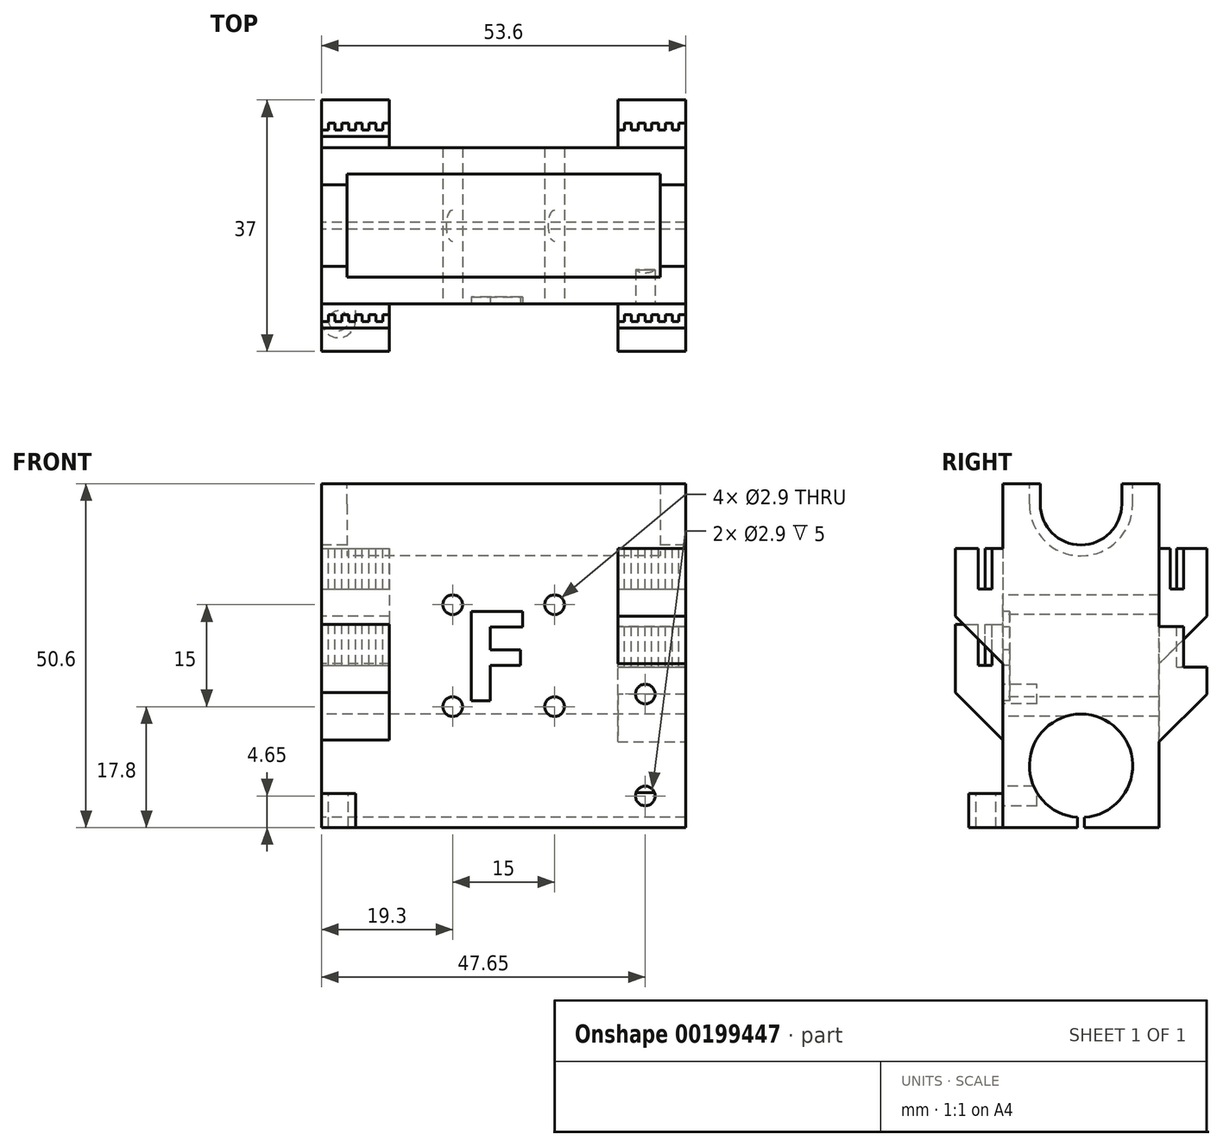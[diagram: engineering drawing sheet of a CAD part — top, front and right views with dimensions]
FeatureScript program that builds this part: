
annotation { "Feature Type Name" : "Feature", "Feature Type Description" : "" }
export const myFeature = defineFeature(function(context is Context, id is Id, definition is map)
    precondition{}
    {
        {
            assignVariable(context, id + "F0", {"name" : "LM8LUU", "anyValue" : 1.8});
        }
        {
            var Q0;
            Q0=qCreatedBy(makeId("Top.planeOp"),FACE);
            var sketch = newSketch(context, id + "F1", { "sketchPlane" : qUnion([Q0])});
            skLineSegment(sketch, "E0.bottom", {"start": v(0, 0) * mm, "end": v(53.6, 0) * mm});
            skLineSegment(sketch, "E0.top", {"start": v(0, 23) * mm, "end": v(53.6, 23) * mm});
            skLineSegment(sketch, "E0.left", {"start": v(0, 0) * mm, "end": v(0, 23) * mm});
            skLineSegment(sketch, "E0.right", {"start": v(53.6, 0) * mm, "end": v(53.6, 23) * mm});
            skSolve(sketch);
        }
        {
            var Q0;
            Q0=qSketchRegion(id+"F1",true);
            extrude(context, id + "F2", {"entities" : qUnion([Q0]), "depth" : 50.6 * mm});
        }
        {
            var Q0;
            Q0=makeQuery(id+"F2.opExtrude","SWEPT_FACE",FACE,{"disambiguationData":[OSD([sQuery(id+"F1.wireOp",EDGE,"E0.left")])]});
            var sketch = newSketch(context, id + "F3", { "sketchPlane" : qUnion([Q0])});
            skCircle(sketch, "E1", {"center": v(-11.5, 9.1) * mm, "radius": 7.6 * mm});
            skCircle(sketch, "E2", {"center": v(-11.5, 47.6) * mm, "radius": 6 * mm});
            skLineSegment(sketch, "E3", {"start": v(-23, 47.6) * mm, "end": v(0, 47.6) * mm, "construction": true});
            skLineSegment(sketch, "E4", {"start": v(-17.5, 50.6) * mm, "end": v(-17.5, 47.6) * mm});
            skLineSegment(sketch, "E5", {"start": v(-5.5, 50.6) * mm, "end": v(-5.5, 47.6) * mm});
            skLineSegment(sketch, "E6", {"start": v(-23, 9.1) * mm, "end": v(0, 9.1) * mm, "construction": true});
            skLineSegment(sketch, "E7", {"start": v(-11.5, 9.1) * mm, "end": v(-11.5, 0) * mm, "construction": true});
            skLineSegment(sketch, "E8", {"start": v(-11.5, 0) * mm, "end": v(-12, 0) * mm});
            skLineSegment(sketch, "E9", {"start": v(-12, 0) * mm, "end": v(-12, 1.52) * mm});
            skLineSegment(sketch, "E10", {"start": v(-12, 1.52) * mm, "end": v(-11, 1.52) * mm});
            skLineSegment(sketch, "E11", {"start": v(-11, 1.52) * mm, "end": v(-11, 0) * mm});
            skLineSegment(sketch, "E12", {"start": v(-11, 0) * mm, "end": v(-11.5, 0) * mm});
            skCircle(sketch, "E13", {"center": v(-11.5, 47.6) * mm, "radius": 7.6 * mm});
            skLineSegment(sketch, "E14", {"start": v(-3.9, 47.6) * mm, "end": v(-3.9, 50.6) * mm});
            skLineSegment(sketch, "E15", {"start": v(-19.1, 47.6) * mm, "end": v(-19.1, 50.6) * mm});
            skSolve(sketch);
        }
        {
            var Q0;
            {var subQ0=sQuery(id+"F3.wireOp",EDGE,"61a55092-bd36-442a-954f-b1d305e603b2");var subQ1=sQuery(id+"F3.wireOp",EDGE,"E1");var subQ3=makeQuery(id+"F3.imprint","INTERSECT",VERTEX,{"disambiguationData":[OD(0.0)],"derivedFrom":[subQ1,subQ0]});Q0=makeQuery(id+"F3.imprint","IMPRINT",FACE,{"disambiguationData":[TD([[makeQuery(id+"F3.imprint","IMPRINT",EDGE,{"disambiguationData":[TD([[subQ3,-1.0]])],"derivedFrom":subQ1}),1.0]])]});}
            var Q1;
            {var subQ0=sQuery(id+"F3.wireOp",EDGE,"ccdeb851-c584-4ba8-b480-4501c20c5f95");var subQ1=sQuery(id+"F3.wireOp",EDGE,"E1");var subQ3=makeQuery(id+"F3.imprint","INTERSECT",VERTEX,{"disambiguationData":[OD(0.0)],"derivedFrom":[subQ1,subQ0]});Q1=makeQuery(id+"F3.imprint","IMPRINT",FACE,{"disambiguationData":[TD([[makeQuery(id+"F3.imprint","IMPRINT",EDGE,{"disambiguationData":[TD([[subQ3,1.0]])],"derivedFrom":subQ1}),1.0]])]});}
            var Q2;
            Q2=makeQuery(id+"F3.imprint","IMPRINT",FACE,{"disambiguationData":[TD([[makeQuery(id+"F3.imprint","IMPRINT",EDGE,{"derivedFrom":sQuery(id+"F3.wireOp",EDGE,"E8")}),-1.0]])]});
            var Q3;
            {var subQ0=sQuery(id+"F3.wireOp",EDGE,"E10");Q3=makeQuery(id+"F3.imprint","IMPRINT",FACE,{"disambiguationData":[TD([[makeQuery(id+"F3.imprint","IMPRINT",EDGE,{"derivedFrom":subQ0}),-1.0]])]});}
            var Q4;
            {var subQ3=sQuery(id+"F3.wireOp",EDGE,"84843404-b723-4df1-a710-1511c094684b");Q4=makeQuery(id+"F3.imprint","IMPRINT",FACE,{"disambiguationData":[TD([[makeQuery(id+"F3.imprint","IMPRINT",EDGE,{"derivedFrom":subQ3}),-1.0]])]});}
            var Q5;
            {var subQ3=sQuery(id+"F3.wireOp",EDGE,"84843404-b723-4df1-a710-1511c094684b");Q5=makeQuery(id+"F3.imprint","IMPRINT",FACE,{"disambiguationData":[TD([[makeQuery(id+"F3.imprint","IMPRINT",EDGE,{"derivedFrom":subQ3}),1.0]])]});}
            var Q6;
            {var subQ7=sQuery(id+"F3.wireOp",EDGE,"E10");Q6=makeQuery(id+"F3.imprint","IMPRINT",FACE,{"disambiguationData":[TD([[makeQuery(id+"F3.imprint","IMPRINT",EDGE,{"derivedFrom":subQ7}),1.0]])]});}
            var Q7;
            {var subQ3=sQuery(id+"F3.wireOp",EDGE,"E5");Q7=makeQuery(id+"F3.imprint","IMPRINT",FACE,{"disambiguationData":[TD([[makeQuery(id+"F3.imprint","IMPRINT",EDGE,{"derivedFrom":subQ3}),-1.0]])]});}
            var Q8;
            {var subQ0=sQuery(id+"F3.wireOp",EDGE,"E4");Q8=makeQuery(id+"F3.imprint","IMPRINT",FACE,{"disambiguationData":[TD([[makeQuery(id+"F3.imprint","IMPRINT",EDGE,{"derivedFrom":subQ0}),1.0]])]});}
            var Q9;
            {var subQ0=sQuery(id+"F3.wireOp",EDGE,"E4");Q9=makeQuery(id+"F3.imprint","IMPRINT",FACE,{"disambiguationData":[TD([[makeQuery(id+"F3.imprint","IMPRINT",EDGE,{"derivedFrom":subQ0}),1.0]])]});}
            var Q10;
            {var subQ3=sQuery(id+"F3.wireOp",EDGE,"E5");Q10=makeQuery(id+"F3.imprint","IMPRINT",FACE,{"disambiguationData":[TD([[makeQuery(id+"F3.imprint","IMPRINT",EDGE,{"derivedFrom":subQ3}),-1.0]])]});}
            var Q11;
            {var subQ1=sQuery(id+"F3.wireOp",EDGE,"E2");var subQ4=makeQuery(id+"F3.imprint","INTERSECT",VERTEX,{"derivedFrom":[subQ1,sQuery(id+"F3.wireOp",EDGE,"E5")]});Q11=makeQuery(id+"F3.imprint","IMPRINT",FACE,{"disambiguationData":[TD([[makeQuery(id+"F3.imprint","IMPRINT",EDGE,{"disambiguationData":[TD([[subQ4,-1.0]])],"derivedFrom":subQ1}),1.0]])]});}
            extrude(context, id + "F4", {"entities" : qUnion([Q0, Q1, Q2, Q3, Q4, Q5, Q6, Q7, Q8, Q9, Q10, Q11]), "operationType" : NewBodyOperationType.REMOVE, "endBound" : BoundingType.THROUGH_ALL, "oppositeDirection" : true, "depth" : 25 * mm});
        }
        {
            var Q0;
            {var subQ3=sQuery(id+"F3.wireOp",EDGE,"E4");Q0=makeQuery(id+"F3.imprint","IMPRINT",FACE,{"disambiguationData":[TD([[makeQuery(id+"F3.imprint","IMPRINT",EDGE,{"derivedFrom":subQ3}),-1.0]])]});}
            var Q1;
            {var subQ3=sQuery(id+"F3.wireOp",EDGE,"E15");Q1=makeQuery(id+"F3.imprint","IMPRINT",FACE,{"disambiguationData":[TD([[makeQuery(id+"F3.imprint","IMPRINT",EDGE,{"derivedFrom":subQ3}),-1.0]])]});}
            var Q2;
            {var subQ3=sQuery(id+"F3.wireOp",EDGE,"E14");Q2=makeQuery(id+"F3.imprint","IMPRINT",FACE,{"disambiguationData":[TD([[makeQuery(id+"F3.imprint","IMPRINT",EDGE,{"derivedFrom":subQ3}),1.0]])]});}
            extrude(context, id + "F5", {"entities" : qUnion([Q0, Q1, Q2]), "operationType" : NewBodyOperationType.REMOVE, "oppositeDirection" : true, "depth" : (46.25 + getVariable(context, 'LM8LUU') * 2) * mm});
        }
        {
            var Q0;
            {var subQ3=sQuery(id+"F3.wireOp",EDGE,"E4");Q0=makeQuery(id+"F3.imprint","IMPRINT",FACE,{"disambiguationData":[TD([[makeQuery(id+"F3.imprint","IMPRINT",EDGE,{"derivedFrom":subQ3}),-1.0]])]});}
            var Q1;
            {var subQ3=sQuery(id+"F3.wireOp",EDGE,"E15");Q1=makeQuery(id+"F3.imprint","IMPRINT",FACE,{"disambiguationData":[TD([[makeQuery(id+"F3.imprint","IMPRINT",EDGE,{"derivedFrom":subQ3}),-1.0]])]});}
            var Q2;
            {var subQ3=sQuery(id+"F3.wireOp",EDGE,"E14");Q2=makeQuery(id+"F3.imprint","IMPRINT",FACE,{"disambiguationData":[TD([[makeQuery(id+"F3.imprint","IMPRINT",EDGE,{"derivedFrom":subQ3}),1.0]])]});}
            extrude(context, id + "F6", {"entities" : qUnion([Q0, Q1, Q2]), "operationType" : NewBodyOperationType.ADD, "oppositeDirection" : true, "depth" : (26.75 - getVariable(context, 'LM8LUU')) * mm});
        }
        {
            var Q0;
            {var subQ3=sQuery(id+"F3.wireOp",EDGE,"E4");Q0=makeQuery(id+"F3.imprint","IMPRINT",FACE,{"disambiguationData":[TD([[makeQuery(id+"F3.imprint","IMPRINT",EDGE,{"derivedFrom":subQ3}),-1.0]])]});}
            var Q1;
            {var subQ3=sQuery(id+"F3.wireOp",EDGE,"E15");Q1=makeQuery(id+"F3.imprint","IMPRINT",FACE,{"disambiguationData":[TD([[makeQuery(id+"F3.imprint","IMPRINT",EDGE,{"derivedFrom":subQ3}),-1.0]])]});}
            var Q2;
            {var subQ3=sQuery(id+"F3.wireOp",EDGE,"E14");Q2=makeQuery(id+"F3.imprint","IMPRINT",FACE,{"disambiguationData":[TD([[makeQuery(id+"F3.imprint","IMPRINT",EDGE,{"derivedFrom":subQ3}),1.0]])]});}
            extrude(context, id + "F7", {"entities" : qUnion([Q0, Q1, Q2]), "operationType" : NewBodyOperationType.REMOVE, "oppositeDirection" : true, "depth" : (23.25 + getVariable(context, 'LM8LUU')) * mm});
        }
        {
            var Q0;
            {var subQ3=sQuery(id+"F3.wireOp",EDGE,"E4");Q0=makeQuery(id+"F3.imprint","IMPRINT",FACE,{"disambiguationData":[TD([[makeQuery(id+"F3.imprint","IMPRINT",EDGE,{"derivedFrom":subQ3}),-1.0]])]});}
            var Q1;
            {var subQ3=sQuery(id+"F3.wireOp",EDGE,"E15");Q1=makeQuery(id+"F3.imprint","IMPRINT",FACE,{"disambiguationData":[TD([[makeQuery(id+"F3.imprint","IMPRINT",EDGE,{"derivedFrom":subQ3}),-1.0]])]});}
            var Q2;
            {var subQ3=sQuery(id+"F3.wireOp",EDGE,"E14");Q2=makeQuery(id+"F3.imprint","IMPRINT",FACE,{"disambiguationData":[TD([[makeQuery(id+"F3.imprint","IMPRINT",EDGE,{"derivedFrom":subQ3}),1.0]])]});}
            extrude(context, id + "F8", {"entities" : qUnion([Q0, Q1, Q2]), "operationType" : NewBodyOperationType.ADD, "oppositeDirection" : true, "depth" : 3.75 * mm});
        }
        {
            var Q0;
            Q0=makeQuery(id+"F2.opExtrude","SWEPT_FACE",FACE,{"disambiguationData":[OSD([sQuery(id+"F1.wireOp",EDGE,"E0.bottom")])]});
            var sketch = newSketch(context, id + "F9", { "sketchPlane" : qUnion([Q0])});
            skLineSegment(sketch, "E16.bottom", {"start": v(0, 29.9) * mm, "end": v(10, 29.9) * mm});
            skLineSegment(sketch, "E16.top", {"start": v(0, 9.9) * mm, "end": v(10, 9.9) * mm});
            skLineSegment(sketch, "E16.left", {"start": v(0, 29.9) * mm, "end": v(0, 9.9) * mm});
            skLineSegment(sketch, "E16.right", {"start": v(10, 29.9) * mm, "end": v(10, 9.9) * mm});
            skLineSegment(sketch, "E17.bottom", {"start": v(53.6, 41.1) * mm, "end": v(43.6, 41.1) * mm});
            skLineSegment(sketch, "E17.top", {"start": v(53.6, 21.1) * mm, "end": v(43.6, 21.1) * mm});
            skLineSegment(sketch, "E17.left", {"start": v(53.6, 41.1) * mm, "end": v(53.6, 21.1) * mm});
            skLineSegment(sketch, "E17.right", {"start": v(43.6, 41.1) * mm, "end": v(43.6, 21.1) * mm});
            skPoint(sketch, "E18", {"position": v(0, 47.6) * mm});
            skPoint(sketch, "E19", {"position": v(0, 9.4) * mm});
            skSolve(sketch);
        }
        {
            var Q0;
            Q0=qSketchRegion(id+"F9",true);
            extrude(context, id + "F10", {"entities" : qUnion([Q0]), "operationType" : NewBodyOperationType.ADD, "depth" : 7 * mm});
        }
        {
            var Q0;
            Q0=makeQuery(id+"F10.opExtrude","CAP_EDGE",EDGE,{"disambiguationData":[OSD([sQuery(id+"F9.wireOp",EDGE,"E16.top")])],"isStart":false});
            var Q1;
            Q1=makeQuery(id+"F10.opExtrude","CAP_EDGE",EDGE,{"disambiguationData":[OSD([sQuery(id+"F9.wireOp",EDGE,"E17.top")])],"isStart":false});
            chamfer(context, id + "F11", {"entities" : qUnion([Q0, Q1]), "width" : 10 * mm, "tangentPropagation" : true});
        }
        {
            var Q0;
            Q0=makeQuery(id+"F10.opExtrude","SWEPT_FACE",FACE,{"disambiguationData":[OSD([sQuery(id+"F9.wireOp",EDGE,"E16.bottom")])]});
            var sketch = newSketch(context, id + "F12", { "sketchPlane" : qUnion([Q0])});
            skLineSegment(sketch, "E20", {"start": v(-935.9, 0) * mm, "end": v(-935.88, -4.54) * mm});
            skLineSegment(sketch, "E21.left", {"start": v(0, -3.6) * mm, "end": v(0, -1.6) * mm});
            skLineSegment(sketch, "E22", {"start": v(6, -2.6) * mm, "end": v(7, -2.6) * mm});
            skLineSegment(sketch, "E23", {"start": v(4, -2.6) * mm, "end": v(5, -2.6) * mm});
            skLineSegment(sketch, "E24", {"start": v(0, -2.6) * mm, "end": v(1, -2.6) * mm});
            skLineSegment(sketch, "E25", {"start": v(7, -1.6) * mm, "end": v(8, -1.6) * mm});
            skLineSegment(sketch, "E26", {"start": v(2, -2.6) * mm, "end": v(3, -2.6) * mm});
            skLineSegment(sketch, "E27", {"start": v(3, -1.6) * mm, "end": v(4, -1.6) * mm});
            skLineSegment(sketch, "E28", {"start": v(8, -2.6) * mm, "end": v(9, -2.6) * mm});
            skLineSegment(sketch, "E29", {"start": v(8, -1.6) * mm, "end": v(8, -2.6) * mm});
            skLineSegment(sketch, "E30", {"start": v(9, -2.6) * mm, "end": v(9, -1.6) * mm});
            skLineSegment(sketch, "E31", {"start": v(10, -1.6) * mm, "end": v(10, -2.6) * mm});
            skLineSegment(sketch, "E32", {"start": v(6, -1.6) * mm, "end": v(6, -2.6) * mm});
            skLineSegment(sketch, "E33", {"start": v(2, -1.6) * mm, "end": v(2, -2.6) * mm});
            skLineSegment(sketch, "E34", {"start": v(1, -1.6) * mm, "end": v(2, -1.6) * mm});
            skLineSegment(sketch, "E35", {"start": v(1, -2.6) * mm, "end": v(1, -1.6) * mm});
            skLineSegment(sketch, "E36", {"start": v(9, -1.6) * mm, "end": v(10, -1.6) * mm});
            skLineSegment(sketch, "E37", {"start": v(5, -1.6) * mm, "end": v(6, -1.6) * mm});
            skLineSegment(sketch, "E38", {"start": v(5, -2.6) * mm, "end": v(5, -1.6) * mm});
            skLineSegment(sketch, "E39", {"start": v(3, -2.6) * mm, "end": v(3, -1.6) * mm});
            skLineSegment(sketch, "E40", {"start": v(4, -1.6) * mm, "end": v(4, -2.6) * mm});
            skLineSegment(sketch, "E41", {"start": v(7, -2.6) * mm, "end": v(7, -1.6) * mm});
            skLineSegment(sketch, "E42", {"start": v(0, -1.6) * mm, "end": v(0, -2.6) * mm});
            skLineSegment(sketch, "E43", {"start": v(10, -2.6) * mm, "end": v(10, -3.6) * mm});
            skLineSegment(sketch, "E44", {"start": v(0, -3.6) * mm, "end": v(10, -3.6) * mm});
            skLineSegment(sketch, "E45", {"start": v(5.3, -1.6) * mm, "end": v(5.3, 0) * mm});
            skSolve(sketch);
        }
        {
            var Q0;
            Q0=qSketchRegion(id+"F12",true);
            extrude(context, id + "F13", {"entities" : qUnion([Q0]), "operationType" : NewBodyOperationType.REMOVE, "oppositeDirection" : true, "depth" : 6 * mm});
        }
        {
            var Q0;
            Q0=makeQuery(id+"F10.opExtrude","SWEPT_FACE",FACE,{"disambiguationData":[OSD([sQuery(id+"F9.wireOp",EDGE,"E17.bottom")])]});
            var sketch = newSketch(context, id + "F14", { "sketchPlane" : qUnion([Q0])});
            skLineSegment(sketch, "E46.left", {"start": v(43.6, -3.6) * mm, "end": v(43.6, -1.6) * mm});
            skLineSegment(sketch, "E47", {"start": v(49.6, -2.6) * mm, "end": v(50.6, -2.6) * mm});
            skLineSegment(sketch, "E48", {"start": v(47.6, -2.6) * mm, "end": v(48.6, -2.6) * mm});
            skLineSegment(sketch, "E49", {"start": v(43.6, -2.6) * mm, "end": v(44.6, -2.6) * mm});
            skLineSegment(sketch, "E50", {"start": v(50.6, -1.6) * mm, "end": v(51.6, -1.6) * mm});
            skLineSegment(sketch, "E51", {"start": v(45.6, -2.6) * mm, "end": v(46.6, -2.6) * mm});
            skLineSegment(sketch, "E52", {"start": v(46.6, -1.6) * mm, "end": v(47.6, -1.6) * mm});
            skLineSegment(sketch, "E53", {"start": v(51.6, -2.6) * mm, "end": v(52.6, -2.6) * mm});
            skLineSegment(sketch, "E54", {"start": v(51.6, -1.6) * mm, "end": v(51.6, -2.6) * mm});
            skLineSegment(sketch, "E55", {"start": v(52.6, -2.6) * mm, "end": v(52.6, -1.6) * mm});
            skLineSegment(sketch, "E56", {"start": v(53.6, -1.6) * mm, "end": v(53.6, -2.6) * mm});
            skLineSegment(sketch, "E57", {"start": v(49.6, -1.6) * mm, "end": v(49.6, -2.6) * mm});
            skLineSegment(sketch, "E58", {"start": v(45.6, -1.6) * mm, "end": v(45.6, -2.6) * mm});
            skLineSegment(sketch, "E59", {"start": v(44.6, -1.6) * mm, "end": v(45.6, -1.6) * mm});
            skLineSegment(sketch, "E60", {"start": v(44.6, -2.6) * mm, "end": v(44.6, -1.6) * mm});
            skLineSegment(sketch, "E61", {"start": v(52.6, -1.6) * mm, "end": v(53.6, -1.6) * mm});
            skLineSegment(sketch, "E62", {"start": v(48.6, -1.6) * mm, "end": v(49.6, -1.6) * mm});
            skLineSegment(sketch, "E63", {"start": v(48.6, -2.6) * mm, "end": v(48.6, -1.6) * mm});
            skLineSegment(sketch, "E64", {"start": v(46.6, -2.6) * mm, "end": v(46.6, -1.6) * mm});
            skLineSegment(sketch, "E65", {"start": v(47.6, -1.6) * mm, "end": v(47.6, -2.6) * mm});
            skLineSegment(sketch, "E66", {"start": v(50.6, -2.6) * mm, "end": v(50.6, -1.6) * mm});
            skLineSegment(sketch, "E67", {"start": v(43.6, -1.6) * mm, "end": v(43.6, -2.6) * mm});
            skLineSegment(sketch, "E68", {"start": v(53.6, -2.6) * mm, "end": v(53.6, -3.6) * mm});
            skLineSegment(sketch, "E69", {"start": v(43.6, -3.6) * mm, "end": v(53.6, -3.6) * mm});
            skLineSegment(sketch, "E70", {"start": v(48.83, -1.6) * mm, "end": v(48.83, 0) * mm});
            skSolve(sketch);
        }
        {
            var Q0;
            Q0=qSketchRegion(id+"F14",true);
            extrude(context, id + "F15", {"entities" : qUnion([Q0]), "operationType" : NewBodyOperationType.REMOVE, "oppositeDirection" : true, "depth" : 6 * mm});
        }
        {
            var Q0;
            Q0=makeQuery(id+"F2.opExtrude","SWEPT_FACE",FACE,{"disambiguationData":[OSD([sQuery(id+"F1.wireOp",EDGE,"E0.top")])]});
            var sketch = newSketch(context, id + "F16", { "sketchPlane" : qUnion([Q0])});
            skLineSegment(sketch, "E71.bottom", {"start": v(-53.6, 9.6) * mm, "end": v(-43.6, 9.6) * mm});
            skLineSegment(sketch, "E71.top", {"start": v(-53.6, 29.6) * mm, "end": v(-43.6, 29.6) * mm});
            skLineSegment(sketch, "E71.left", {"start": v(-53.6, 9.6) * mm, "end": v(-53.6, 29.6) * mm});
            skLineSegment(sketch, "E71.right", {"start": v(-43.6, 9.6) * mm, "end": v(-43.6, 29.6) * mm});
            skLineSegment(sketch, "E72.bottom", {"start": v(0, 41.1) * mm, "end": v(-10, 41.1) * mm});
            skLineSegment(sketch, "E72.top", {"start": v(0, 21.1) * mm, "end": v(-10, 21.1) * mm});
            skLineSegment(sketch, "E72.left", {"start": v(0, 41.1) * mm, "end": v(0, 21.1) * mm});
            skLineSegment(sketch, "E72.right", {"start": v(-10, 41.1) * mm, "end": v(-10, 21.1) * mm});
            skSolve(sketch);
        }
        {
            var Q0;
            Q0=qSketchRegion(id+"F16",true);
            extrude(context, id + "F17", {"entities" : qUnion([Q0]), "operationType" : NewBodyOperationType.ADD, "depth" : 7 * mm});
        }
        {
            var Q0;
            Q0=makeQuery(id+"F17.opExtrude","SWEPT_FACE",FACE,{"disambiguationData":[OSD([sQuery(id+"F16.wireOp",EDGE,"E71.top")])]});
            var sketch = newSketch(context, id + "F18", { "sketchPlane" : qUnion([Q0])});
            skLineSegment(sketch, "E73.left", {"start": v(43.6, 24.6) * mm, "end": v(43.6, 26.6) * mm});
            skLineSegment(sketch, "E74", {"start": v(49.6, 25.6) * mm, "end": v(50.6, 25.6) * mm});
            skLineSegment(sketch, "E75", {"start": v(47.6, 25.6) * mm, "end": v(48.6, 25.6) * mm});
            skLineSegment(sketch, "E76", {"start": v(43.6, 25.6) * mm, "end": v(44.6, 25.6) * mm});
            skLineSegment(sketch, "E77", {"start": v(50.6, 26.6) * mm, "end": v(51.6, 26.6) * mm});
            skLineSegment(sketch, "E78", {"start": v(45.6, 25.6) * mm, "end": v(46.6, 25.6) * mm});
            skLineSegment(sketch, "E79", {"start": v(46.6, 26.6) * mm, "end": v(47.6, 26.6) * mm});
            skLineSegment(sketch, "E80", {"start": v(51.6, 25.6) * mm, "end": v(52.6, 25.6) * mm});
            skLineSegment(sketch, "E81", {"start": v(51.6, 26.6) * mm, "end": v(51.6, 25.6) * mm});
            skLineSegment(sketch, "E82", {"start": v(52.6, 25.6) * mm, "end": v(52.6, 26.6) * mm});
            skLineSegment(sketch, "E83", {"start": v(53.6, 26.6) * mm, "end": v(53.6, 25.6) * mm});
            skLineSegment(sketch, "E84", {"start": v(49.6, 26.6) * mm, "end": v(49.6, 25.6) * mm});
            skLineSegment(sketch, "E85", {"start": v(45.6, 26.6) * mm, "end": v(45.6, 25.6) * mm});
            skLineSegment(sketch, "E86", {"start": v(44.6, 26.6) * mm, "end": v(45.6, 26.6) * mm});
            skLineSegment(sketch, "E87", {"start": v(44.6, 25.6) * mm, "end": v(44.6, 26.6) * mm});
            skLineSegment(sketch, "E88", {"start": v(52.6, 26.6) * mm, "end": v(53.6, 26.6) * mm});
            skLineSegment(sketch, "E89", {"start": v(48.6, 26.6) * mm, "end": v(49.6, 26.6) * mm});
            skLineSegment(sketch, "E90", {"start": v(48.6, 25.6) * mm, "end": v(48.6, 26.6) * mm});
            skLineSegment(sketch, "E91", {"start": v(46.6, 25.6) * mm, "end": v(46.6, 26.6) * mm});
            skLineSegment(sketch, "E92", {"start": v(47.6, 26.6) * mm, "end": v(47.6, 25.6) * mm});
            skLineSegment(sketch, "E93", {"start": v(50.6, 25.6) * mm, "end": v(50.6, 26.6) * mm});
            skLineSegment(sketch, "E94", {"start": v(43.6, 26.6) * mm, "end": v(43.6, 25.6) * mm});
            skLineSegment(sketch, "E95", {"start": v(53.6, 25.6) * mm, "end": v(53.6, 24.6) * mm});
            skLineSegment(sketch, "E96", {"start": v(43.6, 24.6) * mm, "end": v(53.6, 24.6) * mm});
            skLineSegment(sketch, "E97", {"start": v(48.6, 24.6) * mm, "end": v(48.6, 23) * mm});
            skSolve(sketch);
        }
        {
            var Q0;
            {var subQ4=sQuery(id+"F18.wireOp",EDGE,"E73.left");Q0=makeQuery(id+"F18.imprint","IMPRINT",FACE,{"disambiguationData":[TD([[makeQuery(id+"F18.imprint","IMPRINT",EDGE,{"derivedFrom":subQ4}),1.0]])]});}
            extrude(context, id + "F19", {"entities" : qUnion([Q0]), "operationType" : NewBodyOperationType.REMOVE, "oppositeDirection" : true, "depth" : 6 * mm});
        }
        {
            var Q0;
            Q0=makeQuery(id+"F17.opExtrude","SWEPT_FACE",FACE,{"disambiguationData":[OSD([sQuery(id+"F16.wireOp",EDGE,"E72.bottom")])]});
            var sketch = newSketch(context, id + "F20", { "sketchPlane" : qUnion([Q0])});
            skLineSegment(sketch, "E98", {"start": v(6, 25.6) * mm, "end": v(7, 25.6) * mm});
            skLineSegment(sketch, "E99", {"start": v(4, 25.6) * mm, "end": v(5, 25.6) * mm});
            skLineSegment(sketch, "E100", {"start": v(0, 25.6) * mm, "end": v(1, 25.6) * mm});
            skLineSegment(sketch, "E101", {"start": v(7, 26.6) * mm, "end": v(8, 26.6) * mm});
            skLineSegment(sketch, "E102", {"start": v(2, 25.6) * mm, "end": v(3, 25.6) * mm});
            skLineSegment(sketch, "E103", {"start": v(3, 26.6) * mm, "end": v(4, 26.6) * mm});
            skLineSegment(sketch, "E104", {"start": v(8, 25.6) * mm, "end": v(9, 25.6) * mm});
            skLineSegment(sketch, "E105", {"start": v(8, 26.6) * mm, "end": v(8, 25.6) * mm});
            skLineSegment(sketch, "E106", {"start": v(9, 25.6) * mm, "end": v(9, 26.6) * mm});
            skLineSegment(sketch, "E107", {"start": v(10, 26.6) * mm, "end": v(10, 25.6) * mm});
            skLineSegment(sketch, "E108", {"start": v(6, 26.6) * mm, "end": v(6, 25.6) * mm});
            skLineSegment(sketch, "E109", {"start": v(2, 26.6) * mm, "end": v(2, 25.6) * mm});
            skLineSegment(sketch, "E110", {"start": v(1, 26.6) * mm, "end": v(2, 26.6) * mm});
            skLineSegment(sketch, "E111", {"start": v(1, 25.6) * mm, "end": v(1, 26.6) * mm});
            skLineSegment(sketch, "E112", {"start": v(9, 26.6) * mm, "end": v(10, 26.6) * mm});
            skLineSegment(sketch, "E113", {"start": v(5, 26.6) * mm, "end": v(6, 26.6) * mm});
            skLineSegment(sketch, "E114", {"start": v(5, 25.6) * mm, "end": v(5, 26.6) * mm});
            skLineSegment(sketch, "E115", {"start": v(3, 25.6) * mm, "end": v(3, 26.6) * mm});
            skLineSegment(sketch, "E116", {"start": v(4, 26.6) * mm, "end": v(4, 25.6) * mm});
            skLineSegment(sketch, "E117", {"start": v(7, 25.6) * mm, "end": v(7, 26.6) * mm});
            skLineSegment(sketch, "E118", {"start": v(10, 25.6) * mm, "end": v(10, 24.6) * mm});
            skLineSegment(sketch, "E119", {"start": v(0, 24.6) * mm, "end": v(10, 24.6) * mm});
            skLineSegment(sketch, "E120", {"start": v(5, 24.6) * mm, "end": v(5, 23) * mm});
            skLineSegment(sketch, "E121", {"start": v(0, 24.6) * mm, "end": v(0, 25.6) * mm});
            skSolve(sketch);
        }
        {
            var Q0;
            Q0=makeQuery(id+"F20.imprint","IMPRINT",FACE,{"disambiguationData":[TD([[makeQuery(id+"F20.imprint","IMPRINT",EDGE,{"derivedFrom":sQuery(id+"F20.wireOp",EDGE,"E98")}),-1.0]])]});
            extrude(context, id + "F21", {"entities" : qUnion([Q0]), "operationType" : NewBodyOperationType.REMOVE, "oppositeDirection" : true, "depth" : 6 * mm});
        }
        {
            var Q0;
            Q0=makeQuery(id+"F17.opExtrude","CAP_EDGE",EDGE,{"disambiguationData":[OSD([sQuery(id+"F16.wireOp",EDGE,"E72.top")])],"isStart":false});
            var Q1;
            Q1=makeQuery(id+"F17.opExtrude","CAP_EDGE",EDGE,{"disambiguationData":[OSD([sQuery(id+"F16.wireOp",EDGE,"E71.bottom")])],"isStart":false});
            chamfer(context, id + "F22", {"entities" : qUnion([Q0, Q1]), "width" : 10 * mm, "tangentPropagation" : true});
        }
        {
            var Q0;
            Q0=makeQuery(id+"F2.opExtrude","SWEPT_FACE",FACE,{"disambiguationData":[OSD([sQuery(id+"F1.wireOp",EDGE,"E0.bottom")])]});
            var sketch = newSketch(context, id + "F23", { "sketchPlane" : qUnion([Q0])});
            skCircle(sketch, "E122", {"center": v(19.3, 32.8) * mm, "radius": 1.45 * mm});
            skCircle(sketch, "E123", {"center": v(34.3, 32.8) * mm, "radius": 1.45 * mm});
            skCircle(sketch, "E124", {"center": v(19.3, 17.8) * mm, "radius": 1.45 * mm});
            skCircle(sketch, "E125", {"center": v(34.3, 17.8) * mm, "radius": 1.45 * mm});
            skLineSegment(sketch, "E126", {"start": v(19.3, 32.8) * mm, "end": v(0, 32.8) * mm});
            skLineSegment(sketch, "E127", {"start": v(34.3, 17.8) * mm, "end": v(53.6, 17.8) * mm});
            skLineSegment(sketch, "E128", {"start": v(34.3, 32.8) * mm, "end": v(34.3, 50.6) * mm});
            skLineSegment(sketch, "E129", {"start": v(19.3, 17.8) * mm, "end": v(19.3, 0) * mm});
            skCircle(sketch, "E130", {"center": v(26.8, 3.68) * mm, "radius": 1.68 * mm});
            skLineSegment(sketch, "E131", {"start": v(26.8, 0) * mm, "end": v(26.8, 13.82) * mm, "construction": true});
            skSolve(sketch);
        }
        {
            var Q0;
            Q0=makeQuery(id+"F23.imprint","IMPRINT",FACE,{"disambiguationData":[TD([[makeQuery(id+"F23.imprint","IMPRINT",EDGE,{"derivedFrom":sQuery(id+"F23.wireOp",EDGE,"E122")}),1.0]])]});
            var Q1;
            Q1=makeQuery(id+"F23.imprint","IMPRINT",FACE,{"disambiguationData":[TD([[makeQuery(id+"F23.imprint","IMPRINT",EDGE,{"derivedFrom":sQuery(id+"F23.wireOp",EDGE,"E123")}),1.0]])]});
            var Q2;
            Q2=makeQuery(id+"F23.imprint","IMPRINT",FACE,{"disambiguationData":[TD([[makeQuery(id+"F23.imprint","IMPRINT",EDGE,{"derivedFrom":sQuery(id+"F23.wireOp",EDGE,"E124")}),1.0]])]});
            var Q3;
            Q3=makeQuery(id+"F23.imprint","IMPRINT",FACE,{"disambiguationData":[TD([[makeQuery(id+"F23.imprint","IMPRINT",EDGE,{"derivedFrom":sQuery(id+"F23.wireOp",EDGE,"E125")}),1.0]])]});
            var Q4;
            Q4=makeQuery(id+"F23.imprint","IMPRINT",FACE,{"disambiguationData":[TD([[makeQuery(id+"F23.imprint","IMPRINT",EDGE,{"derivedFrom":sQuery(id+"F23.wireOp",EDGE,"E122")}),1.0]])]});
            var Q5;
            Q5=makeQuery(id+"F23.imprint","IMPRINT",FACE,{"disambiguationData":[TD([[makeQuery(id+"F23.imprint","IMPRINT",EDGE,{"derivedFrom":sQuery(id+"F23.wireOp",EDGE,"E123")}),1.0]])]});
            var Q6;
            Q6=makeQuery(id+"F23.imprint","IMPRINT",FACE,{"disambiguationData":[TD([[makeQuery(id+"F23.imprint","IMPRINT",EDGE,{"derivedFrom":sQuery(id+"F23.wireOp",EDGE,"E125")}),1.0]])]});
            var Q7;
            Q7=makeQuery(id+"F23.imprint","IMPRINT",FACE,{"disambiguationData":[TD([[makeQuery(id+"F23.imprint","IMPRINT",EDGE,{"derivedFrom":sQuery(id+"F23.wireOp",EDGE,"E124")}),1.0]])]});
            extrude(context, id + "F24", {"entities" : qUnion([Q0, Q1, Q2, Q3, Q4, Q5, Q6, Q7]), "operationType" : NewBodyOperationType.REMOVE, "endBound" : BoundingType.THROUGH_ALL, "oppositeDirection" : true, "depth" : 25 * mm});
        }
        {
            var Q0;
            Q0=makeQuery(id+"F2.opExtrude","SWEPT_FACE",FACE,{"disambiguationData":[OSD([sQuery(id+"F1.wireOp",EDGE,"E0.bottom")])]});
            var sketch = newSketch(context, id + "F25", { "sketchPlane" : qUnion([Q0])});
            skCircle(sketch, "E132", {"center": v(47.65, 19.65) * mm, "radius": 1.45 * mm});
            skCircle(sketch, "E133", {"center": v(47.65, 4.65) * mm, "radius": 1.45 * mm});
            skSolve(sketch);
        }
        {
            var Q0;
            Q0=qSketchRegion(id+"F25",true);
            extrude(context, id + "F26", {"entities" : qUnion([Q0]), "operationType" : NewBodyOperationType.REMOVE, "oppositeDirection" : true, "depth" : 5 * mm});
        }
        {
            var Q0;
            Q0=makeQuery(id+"F2.opExtrude","SWEPT_FACE",FACE,{"disambiguationData":[OSD([sQuery(id+"F1.wireOp",EDGE,"E0.bottom")])]});
            var sketch = newSketch(context, id + "F27", { "sketchPlane" : qUnion([Q0])});
            skText(sketch, "E134", { "text": "F", "fontName": "OpenSans-Bold.ttf"});
            skLineSegment(sketch, "E135", {"start": v(19.3, 32.8) * mm, "end": v(19.3, 17.8) * mm, "construction": true});
            skLineSegment(sketch, "E136", {"start": v(19.3, 17.8) * mm, "end": v(34.3, 17.8) * mm, "construction": true});
            skLineSegment(sketch, "E137", {"start": v(34.3, 17.8) * mm, "end": v(34.3, 32.8) * mm, "construction": true});
            skLineSegment(sketch, "E138", {"start": v(34.3, 32.8) * mm, "end": v(19.3, 32.8) * mm, "construction": true});
            skLineSegment(sketch, "E139", {"start": v(19.3, 25.3) * mm, "end": v(22.2, 25.3) * mm, "construction": true});
            skLineSegment(sketch, "E140", {"start": v(31.4, 25.3) * mm, "end": v(34.3, 25.3) * mm, "construction": true});
            skLineSegment(sketch, "E141", {"start": v(26.8, 18.66) * mm, "end": v(26.8, 17.8) * mm, "construction": true});
            skLineSegment(sketch, "E142", {"start": v(26.8, 32.8) * mm, "end": v(26.8, 31.94) * mm, "construction": true});
            const initialGuessF27  = {"E134": [0.0204, 0.01866, 1, 0, 0.01328]};
            skSetInitialGuess(sketch, initialGuessF27);
            skSolve(sketch);
        }
        {
            var Q0;
            Q0=qSketchRegion(id+"F27",true);
            extrude(context, id + "F28", {"entities" : qUnion([Q0]), "operationType" : NewBodyOperationType.REMOVE, "oppositeDirection" : true, "depth" : 1 * mm});
        }
        {
            var Q0;
            Q0=makeQuery(id+"F2.opExtrude","SWEPT_FACE",FACE,{"disambiguationData":[OSD([sQuery(id+"F1.wireOp",EDGE,"E0.bottom")])]});
            var sketch = newSketch(context, id + "F29", { "sketchPlane" : qUnion([Q0])});
            skLineSegment(sketch, "E143.bottom", {"start": v(0, 0) * mm, "end": v(5, 0) * mm});
            skLineSegment(sketch, "E143.top", {"start": v(0, 5) * mm, "end": v(5, 5) * mm});
            skLineSegment(sketch, "E143.left", {"start": v(0, 0) * mm, "end": v(0, 5) * mm});
            skLineSegment(sketch, "E143.right", {"start": v(5, 0) * mm, "end": v(5, 5) * mm});
            skSolve(sketch);
        }
        {
            var Q0;
            Q0=qSketchRegion(id+"F29",true);
            extrude(context, id + "F30", {"entities" : qUnion([Q0]), "operationType" : NewBodyOperationType.ADD, "depth" : 5 * mm});
        }
        {
            var Q0;
            Q0=makeQuery(id+"F30.opExtrude","SWEPT_FACE",FACE,{"disambiguationData":[OSD([sQuery(id+"F29.wireOp",EDGE,"E143.top")])]});
            var sketch = newSketch(context, id + "F31", { "sketchPlane" : qUnion([Q0])});
            skCircle(sketch, "E144", {"center": v(2.5, -2.5) * mm, "radius": 1.45 * mm});
            skSolve(sketch);
        }
        {
            var Q0;
            Q0=qSketchRegion(id+"F31",true);
            extrude(context, id + "F32", {"entities" : qUnion([Q0]), "operationType" : NewBodyOperationType.REMOVE, "oppositeDirection" : true, "depth" : 25 * mm});
        }
        {
            var Q0;
            Q0=makeQuery(id+"F30.opExtrude","CAP_EDGE",EDGE,{"disambiguationData":[OSD([sQuery(id+"F29.wireOp",EDGE,"E143.left")])],"isStart":false});
            var Q1;
            Q1=makeQuery(id+"F30.opExtrude","CAP_EDGE",EDGE,{"disambiguationData":[OSD([sQuery(id+"F29.wireOp",EDGE,"E143.right")])],"isStart":false});
            fillet(context, id + "F33", {"entities" : qUnion([Q0, Q1]), "radius" : 2.5 * mm, "tangentPropagation" : true, "allowEdgeOverflow" : false});
        }
    });
